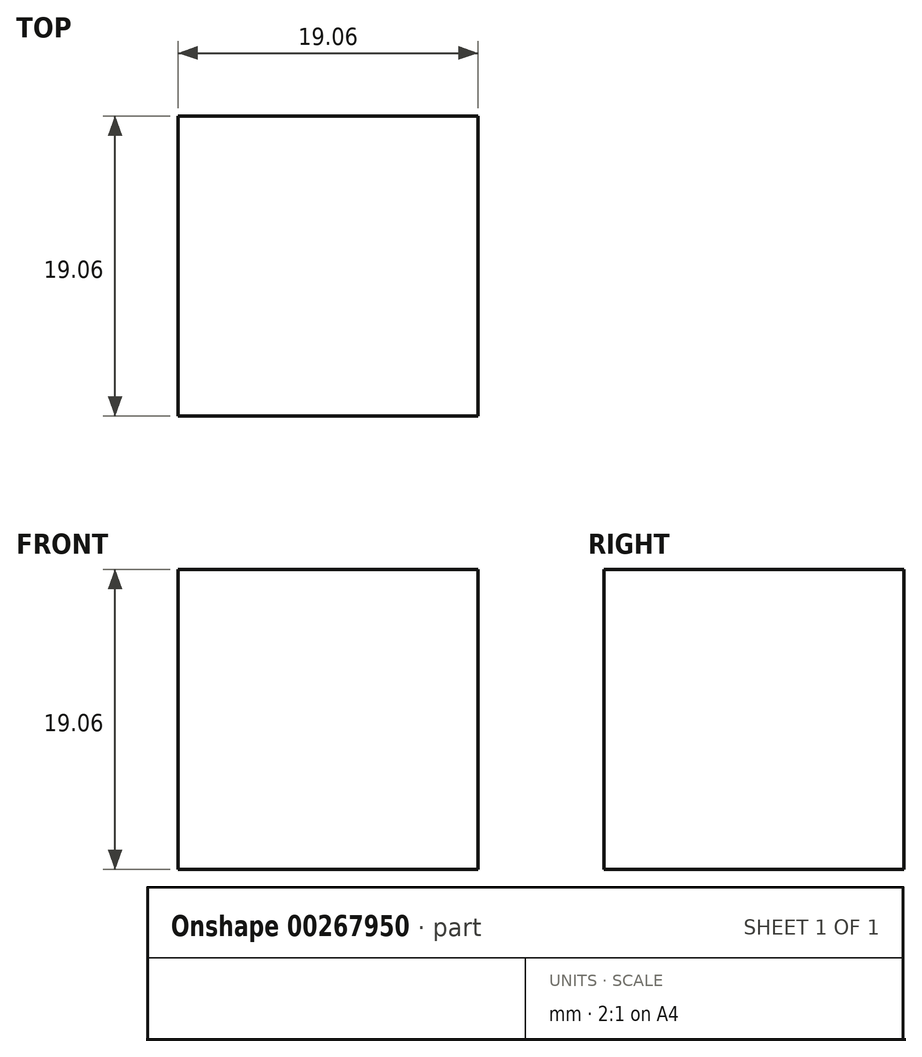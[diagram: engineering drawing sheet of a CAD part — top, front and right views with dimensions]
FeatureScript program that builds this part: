
annotation { "Feature Type Name" : "Feature", "Feature Type Description" : "" }
export const myFeature = defineFeature(function(context is Context, id is Id, definition is map)
    precondition{}
    {
        {
            var Q0;
            Q0=qCreatedBy(makeId("Front.planeOp"),FACE);
            var sketch = newSketch(context, id + "F0", { "sketchPlane" : qUnion([Q0])});
            skLineSegment(sketch, "E0.bottom", {"start": v(9.53, 9.52) * mm, "end": v(-9.52, 9.52) * mm});
            skLineSegment(sketch, "E0.top", {"start": v(9.53, -9.53) * mm, "end": v(-9.52, -9.53) * mm});
            skLineSegment(sketch, "E0.left", {"start": v(9.53, 9.52) * mm, "end": v(9.53, -9.53) * mm});
            skLineSegment(sketch, "E0.right", {"start": v(-9.52, 9.53) * mm, "end": v(-9.52, -9.53) * mm});
            skPoint(sketch, "E0.middle", {"position": v(0, 0) * mm});
            skSolve(sketch);
        }
        {
            var Q0;
            Q0 = qSketchRegion(id + "F0", true);
            extrude(context, id + "F1", {"entities" : qUnion([Q0]), "endBound" : BoundingType.SYMMETRIC, "depth" : 19.05 * mm});
        }
    });
